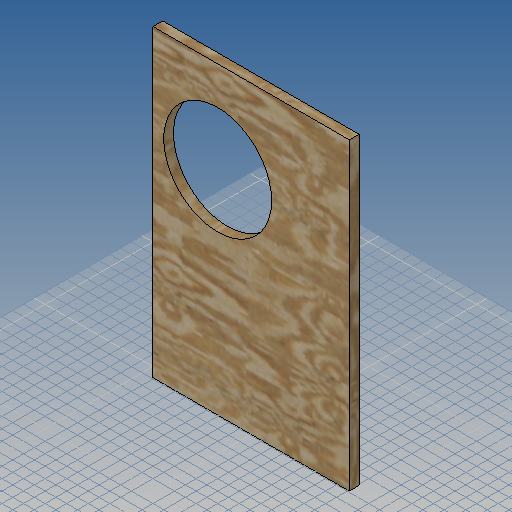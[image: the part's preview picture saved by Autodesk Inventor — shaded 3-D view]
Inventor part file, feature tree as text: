
AUTODESK INVENTOR PART (.ipt)
format: ipt  version: 2019 (Build 230136000, 136)  size: 269,312 bytes
history: native  units: mm
features: other x1, extrude x1, sketch x1
ambient origin geometry x8: Origin, YZ Plane, XZ Plane, XY Plane, X Axis, Y Axis, Z Axis, Center Point
bodies: Volumenkörper1 (feature_tree)
feature tree (3):
  other  "<userpath>\OneDrive\Dokumente\Inventor\Absauganlage\Absauganlage_Params.xlsx"
  extrude  "Extrusion1"  Depth=564.0mm
  sketch  "Skizze1"  dims[d0=364.0mm d1=564.0mm d2=18.0mm d3=0.0mm d4=200.0mm d5=170.0mm d6=120.0mm]
